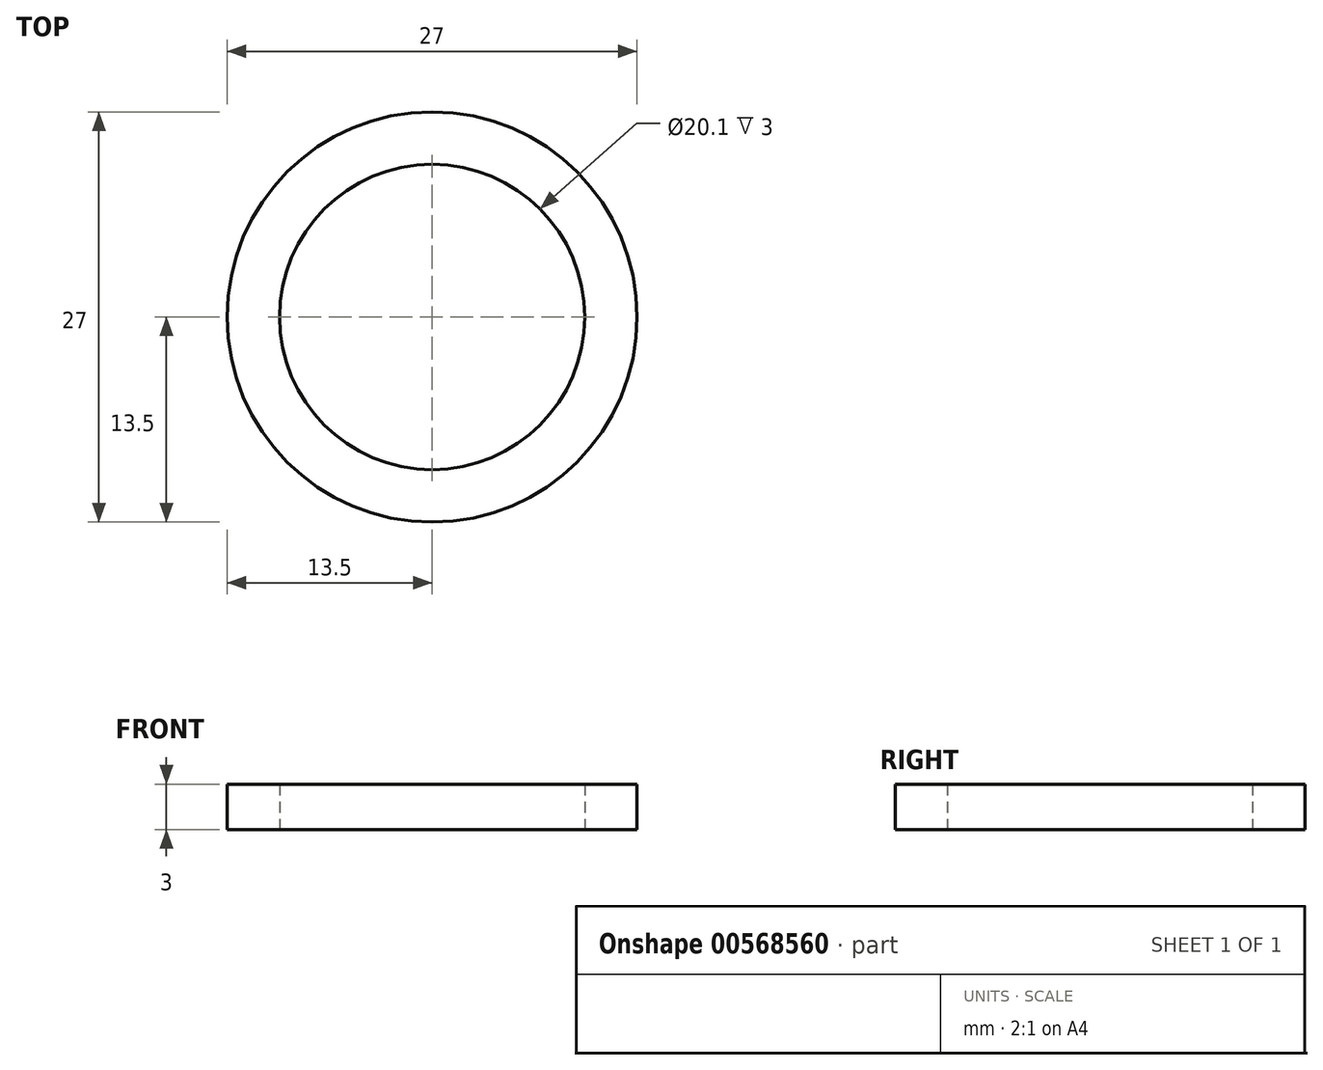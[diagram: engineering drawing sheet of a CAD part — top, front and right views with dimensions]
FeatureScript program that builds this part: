
annotation { "Feature Type Name" : "Feature", "Feature Type Description" : "" }
export const myFeature = defineFeature(function(context is Context, id is Id, definition is map)
    precondition{}
    {
        {
            var Q0;
            Q0=qCreatedBy(makeId("Top.planeOp"),FACE);
            var sketch = newSketch(context, id + "F0", { "sketchPlane" : qUnion([Q0])});
            skCircle(sketch, "E0", {"center": v(0, 0) * mm, "radius": 10.05 * mm});
            skCircle(sketch, "E1", {"center": v(0, 0) * mm, "radius": 13.5 * mm});
            skSolve(sketch);
        }
        {
            var Q0;
            Q0=makeQuery(id+"F0.imprint","IMPRINT",FACE,{"disambiguationData":[TD([[makeQuery(id+"F0.imprint","IMPRINT",EDGE,{"derivedFrom":sQuery(id+"F0.wireOp",EDGE,"E0")}),-1.0]])]});
            extrude(context, id + "F1", {"entities" : qUnion([Q0]), "depth" : 3 * mm, "offsetDistance" : 25 * mm});
        }
    });
